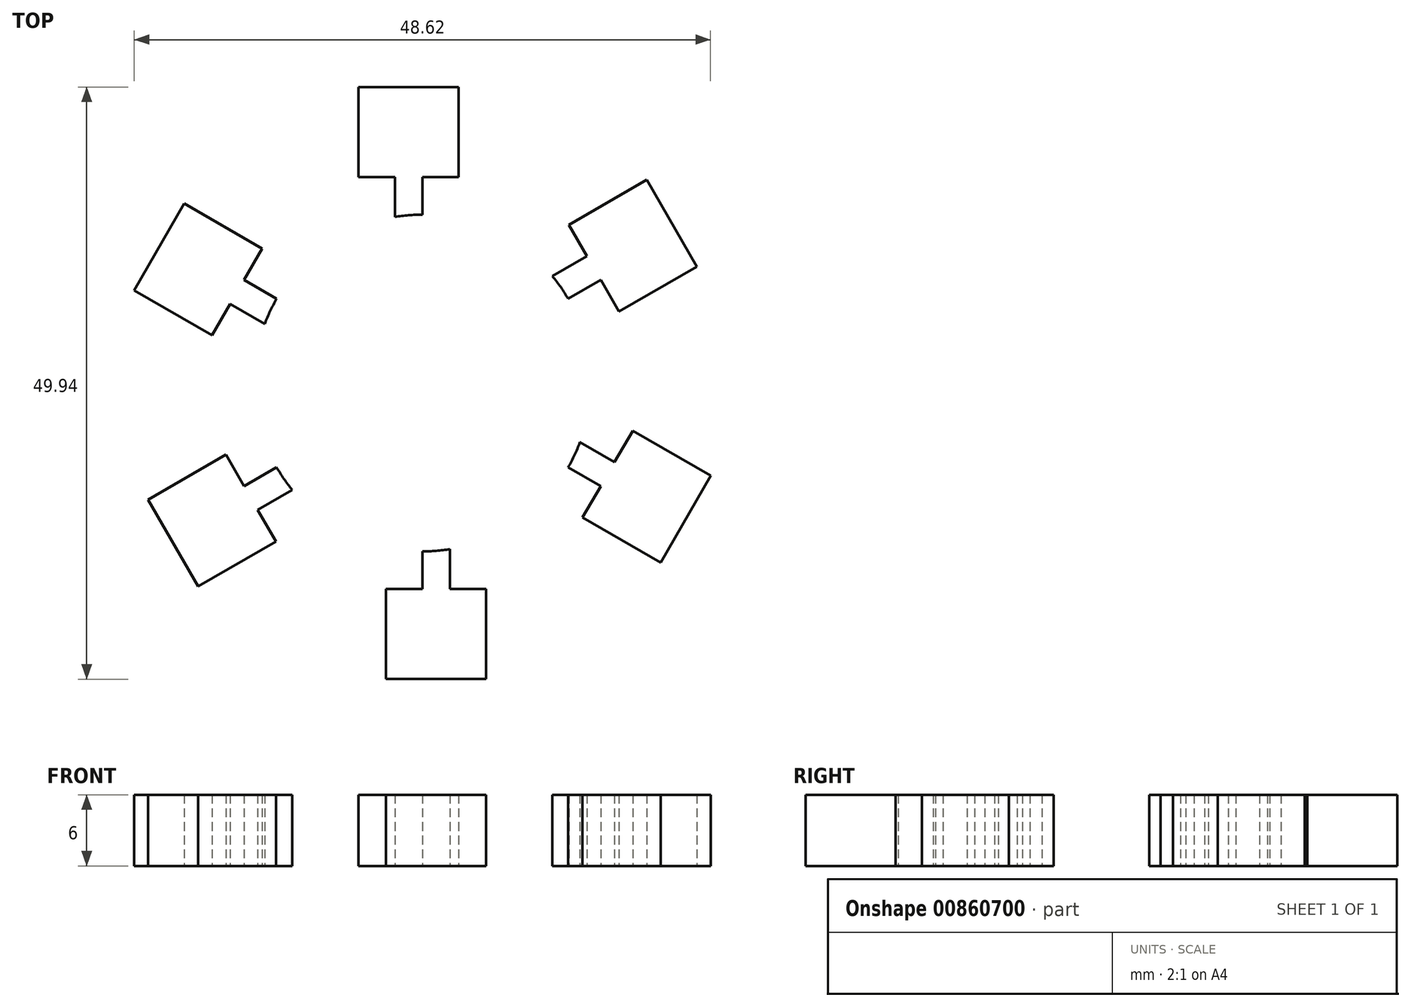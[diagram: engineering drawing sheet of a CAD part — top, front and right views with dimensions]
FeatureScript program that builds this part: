
annotation { "Feature Type Name" : "Feature", "Feature Type Description" : "" }
export const myFeature = defineFeature(function(context is Context, id is Id, definition is map)
    precondition{}
    {
        {
            var Q0;
            Q0=qCreatedBy(makeId("Top.planeOp"),FACE);
            var sketch = newSketch(context, id + "F0", { "sketchPlane" : qUnion([Q0])});
            skCircle(sketch, "E0", {"center": v(0, 0) * mm, "radius": 11.2 * mm});
            skCircle(sketch, "E1", {"center": v(0, 0) * mm, "radius": 14.2 * mm});
            skLineSegment(sketch, "E2", {"start": v(-2.32, 14) * mm, "end": v(-2.32, 17.37) * mm});
            skLineSegment(sketch, "E3", {"start": v(0, 17.37) * mm, "end": v(0, 14.2) * mm});
            skLineSegment(sketch, "E4", {"start": v(0, 17.37) * mm, "end": v(3.07, 17.37) * mm});
            skLineSegment(sketch, "E5", {"start": v(-2.32, 17.37) * mm, "end": v(-5.39, 17.37) * mm});
            skLineSegment(sketch, "E6", {"start": v(-5.39, 17.37) * mm, "end": v(-5.39, 24.97) * mm});
            skLineSegment(sketch, "E7", {"start": v(-5.39, 24.97) * mm, "end": v(0, 24.97) * mm});
            skLineSegment(sketch, "E8", {"start": v(0, 24.97) * mm, "end": v(3.07, 24.97) * mm});
            skLineSegment(sketch, "E9", {"start": v(3.07, 24.97) * mm, "end": v(3.07, 17.37) * mm});
            skLineSegment(sketch, "E10.1.0", {"start": v(-24.31, 7.82) * mm, "end": v(-21.62, 12.48) * mm});
            skLineSegment(sketch, "E10.1.1", {"start": v(-21.62, 12.48) * mm, "end": v(-20.09, 15.14) * mm});
            skLineSegment(sketch, "E10.1.2", {"start": v(-20.09, 15.14) * mm, "end": v(-13.51, 11.34) * mm});
            skLineSegment(sketch, "E10.1.3", {"start": v(-15.05, 8.69) * mm, "end": v(-13.51, 11.34) * mm});
            skLineSegment(sketch, "E10.1.4", {"start": v(-17.74, 4.02) * mm, "end": v(-24.31, 7.82) * mm});
            skLineSegment(sketch, "E10.1.5", {"start": v(-16.2, 6.68) * mm, "end": v(-17.74, 4.02) * mm});
            skLineSegment(sketch, "E10.1.6", {"start": v(-13.3, 5) * mm, "end": v(-16.2, 6.68) * mm});
            skLineSegment(sketch, "E10.1.7", {"start": v(-15.05, 8.69) * mm, "end": v(-12.3, 7.1) * mm});
            skLineSegment(sketch, "E10.2.0", {"start": v(-18.93, -17.15) * mm, "end": v(-21.62, -12.48) * mm});
            skLineSegment(sketch, "E10.2.1", {"start": v(-21.62, -12.48) * mm, "end": v(-23.15, -9.83) * mm});
            skLineSegment(sketch, "E10.2.2", {"start": v(-23.15, -9.83) * mm, "end": v(-16.58, -6.03) * mm});
            skLineSegment(sketch, "E10.2.3", {"start": v(-15.05, -8.69) * mm, "end": v(-16.58, -6.03) * mm});
            skLineSegment(sketch, "E10.2.4", {"start": v(-12.35, -13.35) * mm, "end": v(-18.93, -17.15) * mm});
            skLineSegment(sketch, "E10.2.5", {"start": v(-13.89, -10.7) * mm, "end": v(-12.35, -13.35) * mm});
            skLineSegment(sketch, "E10.2.6", {"start": v(-10.97, -9.01) * mm, "end": v(-13.89, -10.7) * mm});
            skLineSegment(sketch, "E10.2.7", {"start": v(-15.05, -8.69) * mm, "end": v(-12.3, -7.1) * mm});
            skLineSegment(sketch, "E10.3.0", {"start": v(5.39, -24.97) * mm, "end": v(0, -24.97) * mm});
            skLineSegment(sketch, "E10.3.1", {"start": v(0, -24.97) * mm, "end": v(-3.07, -24.97) * mm});
            skLineSegment(sketch, "E10.3.2", {"start": v(-3.07, -24.97) * mm, "end": v(-3.07, -17.37) * mm});
            skLineSegment(sketch, "E10.3.3", {"start": v(0, -17.37) * mm, "end": v(-3.07, -17.37) * mm});
            skLineSegment(sketch, "E10.3.4", {"start": v(5.39, -17.37) * mm, "end": v(5.39, -24.97) * mm});
            skLineSegment(sketch, "E10.3.5", {"start": v(2.32, -17.37) * mm, "end": v(5.39, -17.37) * mm});
            skLineSegment(sketch, "E10.3.6", {"start": v(2.32, -14) * mm, "end": v(2.32, -17.37) * mm});
            skLineSegment(sketch, "E10.3.7", {"start": v(0, -17.37) * mm, "end": v(0, -14.2) * mm});
            skLineSegment(sketch, "E10.4.0", {"start": v(24.31, -7.82) * mm, "end": v(21.62, -12.48) * mm});
            skLineSegment(sketch, "E10.4.1", {"start": v(21.62, -12.48) * mm, "end": v(20.09, -15.14) * mm});
            skLineSegment(sketch, "E10.4.2", {"start": v(20.09, -15.14) * mm, "end": v(13.51, -11.34) * mm});
            skLineSegment(sketch, "E10.4.3", {"start": v(15.05, -8.69) * mm, "end": v(13.51, -11.34) * mm});
            skLineSegment(sketch, "E10.4.4", {"start": v(17.74, -4.02) * mm, "end": v(24.31, -7.82) * mm});
            skLineSegment(sketch, "E10.4.5", {"start": v(16.2, -6.68) * mm, "end": v(17.74, -4.02) * mm});
            skLineSegment(sketch, "E10.4.6", {"start": v(13.3, -5) * mm, "end": v(16.2, -6.68) * mm});
            skLineSegment(sketch, "E10.4.7", {"start": v(15.05, -8.69) * mm, "end": v(12.3, -7.1) * mm});
            skLineSegment(sketch, "E10.5.0", {"start": v(18.93, 17.15) * mm, "end": v(21.62, 12.48) * mm});
            skLineSegment(sketch, "E10.5.1", {"start": v(21.62, 12.48) * mm, "end": v(23.15, 9.83) * mm});
            skLineSegment(sketch, "E10.5.2", {"start": v(23.15, 9.83) * mm, "end": v(16.58, 6.03) * mm});
            skLineSegment(sketch, "E10.5.3", {"start": v(15.05, 8.69) * mm, "end": v(16.58, 6.03) * mm});
            skLineSegment(sketch, "E10.5.4", {"start": v(12.35, 13.35) * mm, "end": v(18.93, 17.15) * mm});
            skLineSegment(sketch, "E10.5.5", {"start": v(13.89, 10.7) * mm, "end": v(12.35, 13.35) * mm});
            skLineSegment(sketch, "E10.5.6", {"start": v(10.97, 9.01) * mm, "end": v(13.89, 10.7) * mm});
            skLineSegment(sketch, "E10.5.7", {"start": v(15.05, 8.69) * mm, "end": v(12.3, 7.1) * mm});
            skSolve(sketch);
        }
        {
            var Q0;
            {var subQ1=sQuery(id+"F0.wireOp",EDGE,"E2");Q0=makeQuery(id+"F0.imprint","IMPRINT",FACE,{"disambiguationData":[TD([[makeQuery(id+"F0.imprint","IMPRINT",EDGE,{"derivedFrom":subQ1}),-1.0]])]});}
            var Q1;
            Q1=makeQuery(id+"F0.imprint","IMPRINT",FACE,{"disambiguationData":[TD([[makeQuery(id+"F0.imprint","IMPRINT",EDGE,{"derivedFrom":sQuery(id+"F0.wireOp",EDGE,"E10.5.0")}),-1.0]])]});
            var Q2;
            Q2=makeQuery(id+"F0.imprint","IMPRINT",FACE,{"disambiguationData":[TD([[makeQuery(id+"F0.imprint","IMPRINT",EDGE,{"derivedFrom":sQuery(id+"F0.wireOp",EDGE,"E10.4.0")}),-1.0]])]});
            var Q3;
            Q3=makeQuery(id+"F0.imprint","IMPRINT",FACE,{"disambiguationData":[TD([[makeQuery(id+"F0.imprint","IMPRINT",EDGE,{"derivedFrom":sQuery(id+"F0.wireOp",EDGE,"E10.3.0")}),-1.0]])]});
            var Q4;
            Q4=makeQuery(id+"F0.imprint","IMPRINT",FACE,{"disambiguationData":[TD([[makeQuery(id+"F0.imprint","IMPRINT",EDGE,{"derivedFrom":sQuery(id+"F0.wireOp",EDGE,"E10.2.0")}),-1.0]])]});
            var Q5;
            Q5=makeQuery(id+"F0.imprint","IMPRINT",FACE,{"disambiguationData":[TD([[makeQuery(id+"F0.imprint","IMPRINT",EDGE,{"derivedFrom":sQuery(id+"F0.wireOp",EDGE,"E10.1.0")}),-1.0]])]});
            extrude(context, id + "F1", {"entities" : qUnion([Q0, Q1, Q2, Q3, Q4, Q5]), "depth" : 6 * mm, "offsetDistance" : 25 * mm});
        }
    });
